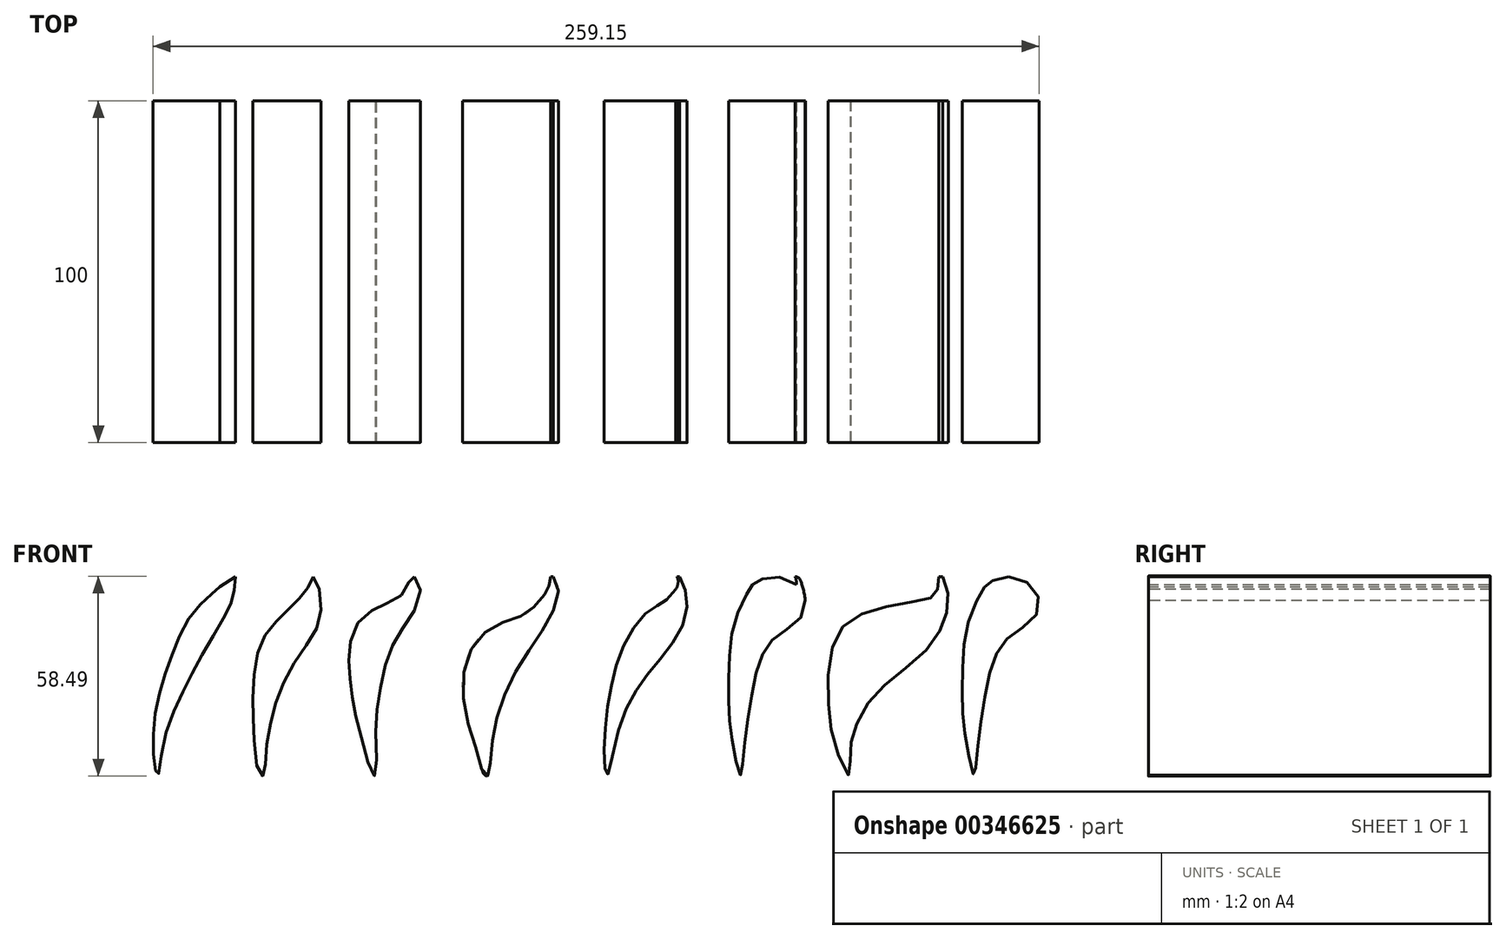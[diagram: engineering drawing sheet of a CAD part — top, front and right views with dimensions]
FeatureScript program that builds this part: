
annotation { "Feature Type Name" : "Feature", "Feature Type Description" : "" }
export const myFeature = defineFeature(function(context is Context, id is Id, definition is map)
    precondition{}
    {
        {
            var Q0;
            Q0=qCreatedBy(makeId("Front.planeOp"),FACE);
            var sketch = newSketch(context, id + "F0", { "sketchPlane" : qUnion([Q0])});
            skLineSegment(sketch, "E0", {"start": v(-127.74, 58) * mm, "end": v(159.03, 58) * mm, "construction": true});
            skFitSpline(sketch, "E1", {"points": [v(25.57, 58) * mm, v(27, 53.87) * mm, v(24.5, 45.98) * mm, v(18.76, 37) * mm, v(12.66, 26.6) * mm, v(8.7, 15.83) * mm, v(7.27, 5.79) * mm, v(6.56, 0) * mm, v(6.33, -0.2) * mm, v(5.48, 0) * mm, v(3.33, 6.5) * mm, v(0, 17.48) * mm, v(-0.64, 30.53) * mm, v(3.69, 39.91) * mm, v(10.5, 44.58) * mm, v(16.6, 46.72) * mm, v(20.55, 49.96) * mm, v(23.42, 53.55) * mm, v(24.1, 54.93) * mm, v(24.56, 56.63) * mm, v(24.75, 58) * mm], "startDerivative": vector(47.73, -86.57) * mm, "endDerivative": vector(2.68, 50.18) * mm});
            skLineSegment(sketch, "E2", {"start": v(24.75, 58) * mm, "end": v(25.57, 58) * mm});
            skFitSpline(sketch, "E3", {"points": [v(-15.16, 58) * mm, v(-13.4, 54.17) * mm, v(-16.58, 45.7) * mm, v(-20.81, 39.34) * mm, v(-24, 30.86) * mm, v(-25.76, 20.97) * mm, v(-26.47, 11.08) * mm, v(-26.47, 0) * mm, v(-27.17, 0) * mm, v(-30.01, 8.61) * mm, v(-32.47, 18.14) * mm, v(-33.53, 25.2) * mm, v(-34.24, 31.57) * mm, v(-33.88, 38.63) * mm, v(-30.7, 45.7) * mm, v(-25.4, 49.22) * mm, v(-20.81, 51.34) * mm, v(-17.28, 54.68) * mm, v(-16.31, 58) * mm, v(-15.16, 58) * mm]});
            skFitSpline(sketch, "E4", {"points": [v(-44.7, 58) * mm, v(-42.73, 53.15) * mm, v(-43.28, 44.04) * mm, v(-48.23, 35.91) * mm, v(-53.88, 26.03) * mm, v(-57.06, 15.78) * mm, v(-58.6, 5.24) * mm, v(-59.18, 0) * mm, v(-60.25, 0) * mm, v(-62.03, 11.11) * mm, v(-62.35, 21.43) * mm, v(-61.42, 33.7) * mm, v(-58.12, 41.92) * mm, v(-53.17, 47.22) * mm, v(-48.93, 51.45) * mm, v(-46.22, 55.03) * mm, v(-44.7, 58) * mm]});
            skFitSpline(sketch, "E5", {"points": [v(-67.42, 58) * mm, v(-68.13, 52.26) * mm, v(-70.86, 46) * mm, v(-77.58, 34.45) * mm, v(-83.46, 23.11) * mm, v(-88.61, 8.82) * mm, v(-90.1, 0) * mm, v(-90.8, 1.55) * mm, v(-91.5, 11.6) * mm, v(-89.67, 24) * mm, v(-85.78, 35.66) * mm, v(-80.84, 46.25) * mm, v(-74.84, 52.6) * mm, v(-72.01, 55.08) * mm], "startDerivative": vector(-3.13, -86.86) * mm, "endDerivative": vector(50, 43.55) * mm});
            skLineSegment(sketch, "E6", {"start": v(-72.01, 55.08) * mm, "end": v(-67.42, 58) * mm});
            skFitSpline(sketch, "E7", {"points": [v(62.48, 58) * mm, v(64.6, 52.24) * mm, v(62.83, 42.7) * mm, v(56.12, 33.17) * mm, v(49.5, 24.34) * mm, v(44.11, 11.27) * mm, v(41.26, 0) * mm, v(40.55, 2.5) * mm, v(40.8, 14.48) * mm, v(42.7, 27.17) * mm, v(46.59, 38.82) * mm, v(52.59, 47.3) * mm, v(56.83, 50.12) * mm, v(60, 52.6) * mm, v(61.7, 58) * mm], "startDerivative": vector(44.86, -85.59) * mm, "endDerivative": vector(-56.06, 102.68) * mm});
            skFitSpline(sketch, "E8", {"points": [v(61.7, 58) * mm, v(61.4, 54.4) * mm], "startDerivative": vector(1.62, -3.29) * mm, "endDerivative": vector(-2.28, -4.38) * mm});
            skLineSegment(sketch, "E9", {"start": v(61.7, 58) * mm, "end": v(62.48, 58) * mm});
            skFitSpline(sketch, "E10", {"points": [v(90.38, 58) * mm, v(98.15, 54.15) * mm, v(98.15, 46.39) * mm, v(90.77, 40.64) * mm, v(86.02, 33.65) * mm, v(82.96, 19.9) * mm, v(81.03, 5.18) * mm, v(80.28, 0) * mm, v(78.28, 7.68) * mm, v(76.96, 18.48) * mm, v(76.96, 31.9) * mm, v(78.72, 45.33) * mm, v(82.96, 54.5) * mm, v(84.58, 56.34) * mm, v(90.38, 58) * mm]});
            skFitSpline(sketch, "E11", {"points": [v(99.23, 50.99) * mm, v(97.99, 56.5) * mm, v(96.24, 58) * mm], "startDerivative": vector(-0.77, 9.43) * mm, "endDerivative": vector(-8.79, 0) * mm});
            skFitSpline(sketch, "E12", {"points": [v(96.64, 55.8) * mm, v(96.6, 56.68) * mm, v(96.52, 57.27) * mm, v(96.24, 58) * mm], "startDerivative": vector(-0.5, 2.99) * mm, "endDerivative": vector(-1.2, 2.3) * mm});
            skFitSpline(sketch, "E13", {"points": [v(139.42, 58) * mm, v(141.02, 52.26) * mm, v(139.96, 45.55) * mm, v(135.72, 37.78) * mm, v(125.13, 28.6) * mm, v(117, 20.12) * mm, v(113.12, 11.64) * mm, v(112.41, 5.64) * mm, v(112.06, 0) * mm, v(108.18, 8.1) * mm, v(106.06, 20.12) * mm, v(106.76, 36) * mm, v(111.7, 44.84) * mm, v(121.95, 49.08) * mm, v(133.6, 51.2) * mm, v(137.19, 52.56) * mm, v(138.07, 54.86) * mm, v(138.25, 58) * mm], "startDerivative": vector(66.74, -41.17) * mm, "endDerivative": vector(-26.52, 132.57) * mm});
            skLineSegment(sketch, "E14", {"start": v(138.25, 58) * mm, "end": v(139.42, 58) * mm});
            skFitSpline(sketch, "E15", {"points": [v(158.72, 58) * mm, v(166.5, 54.15) * mm, v(166.5, 46.39) * mm, v(159.11, 40.64) * mm, v(154.37, 33.65) * mm, v(151.3, 19.9) * mm, v(149.37, 5.18) * mm, v(148.62, 0) * mm, v(146.62, 7.68) * mm, v(145.3, 18.48) * mm, v(145.3, 31.9) * mm, v(147.07, 45.33) * mm, v(151.3, 54.5) * mm, v(152.92, 56.34) * mm, v(158.72, 58) * mm]});
            skSolve(sketch);
        }
        {
            var Q0;
            Q0 = qSketchRegion(id + "F0", true);
            extrude(context, id + "F1", {"entities" : qUnion([Q0]), "depth" : 100 * mm});
        }
    });
